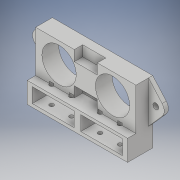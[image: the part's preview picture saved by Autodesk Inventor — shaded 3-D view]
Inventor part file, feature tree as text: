
AUTODESK INVENTOR PART (.ipt)
format: ipt  version: 2019 (Build 230136000, 136)  size: 216,064 bytes
history: native  units: mm
features: sketch x7, extrude x5, projected_geometry x3, hole x2, other x1
ambient origin geometry x8: Origin, YZ Plane, XZ Plane, XY Plane, X Axis, Y Axis, Z Axis, Center Point
bodies: Body1 (feature_tree)
feature tree (18):
  other  "Твердое тело1"
  extrude  "Выдавливание1"  Depth=20.0mm
  extrude  "Выдавливание2"  Depth=48.0mm
  extrude  "Выдавливание3"  Depth=4.0mm
  extrude  "Выдавливание4"  Depth=55.0mm
  hole  "Отверстие1"  [1 undecoded]
  extrude  "Выдавливание5"  Depth=6.0mm TaperAngle=0.0deg
  hole  "Отверстие2"  [1 undecoded]
  sketch  "Эскиз1"
  sketch  "Эскиз2"
  sketch  "Эскиз3"
  sketch  "Эскиз4"
  sketch  "Эскиз5"
  sketch  "Эскиз6"
  sketch  "Эскиз7"
  projected_geometry  "Спроецированная петля1"
  projected_geometry  "Спроецированная петля2"
  projected_geometry  "Спроецированная петля3"
note: 2 required parameter values undecoded (feature->parameter linkage not recoverable at this tier; creation-order binding heuristic only, values carry confidence <= 0.55)
